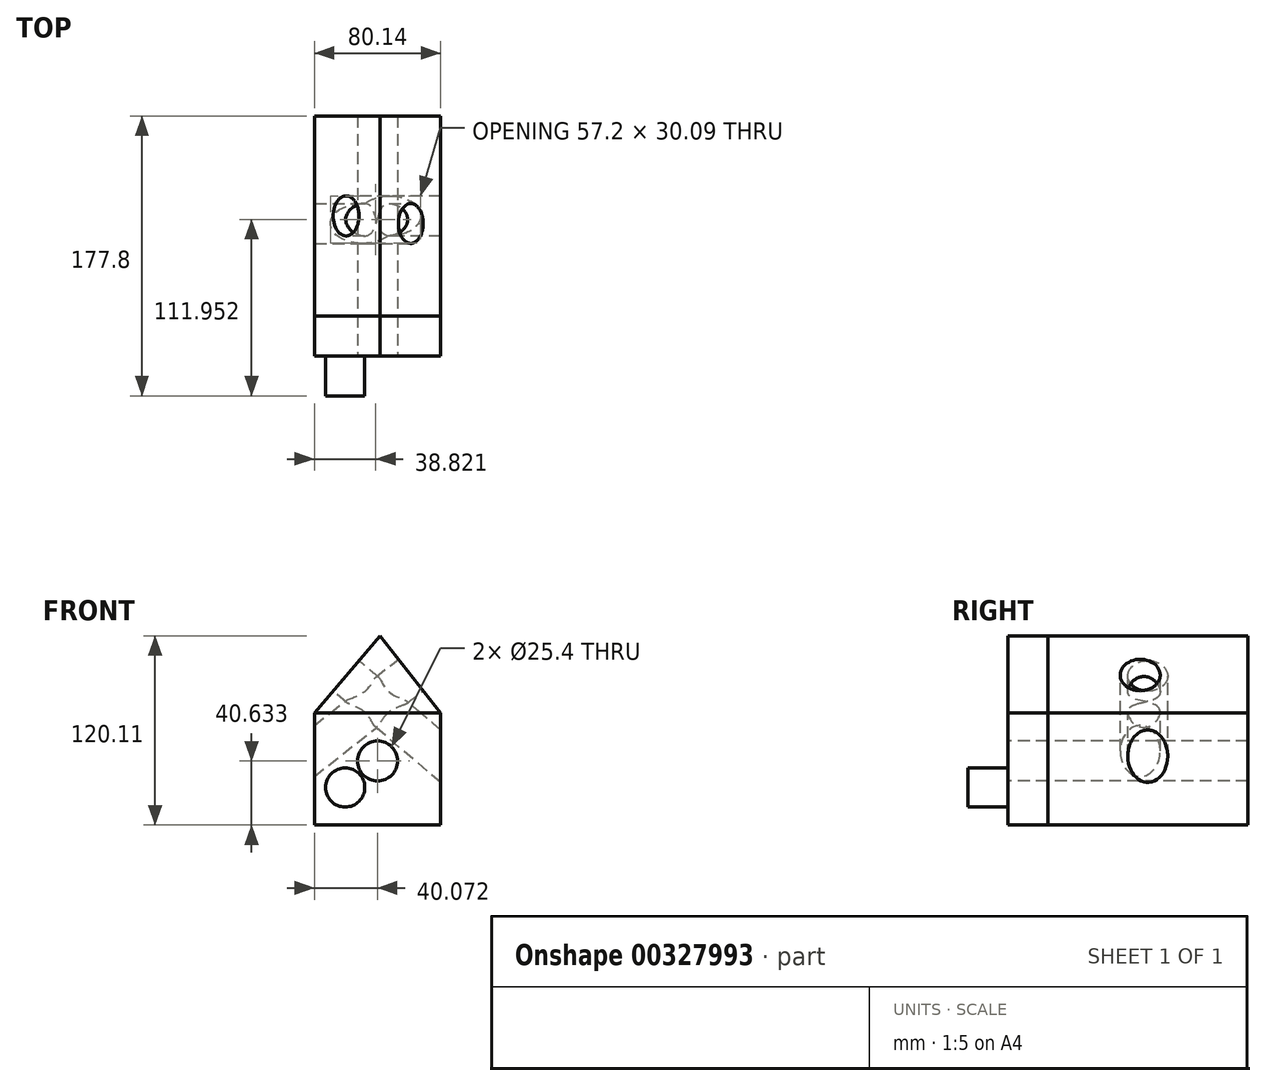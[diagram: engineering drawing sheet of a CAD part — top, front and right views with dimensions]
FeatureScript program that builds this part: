
annotation { "Feature Type Name" : "Feature", "Feature Type Description" : "" }
export const myFeature = defineFeature(function(context is Context, id is Id, definition is map)
    precondition{}
    {
        {
            var Q0;
            Q0=qCreatedBy(makeId("Front.planeOp"),FACE);
            var sketch = newSketch(context, id + "F0", { "sketchPlane" : qUnion([Q0])});
            skLineSegment(sketch, "E0.bottom", {"start": v(-274.23, -72.35) * mm, "end": v(-194.09, -72.35) * mm});
            skLineSegment(sketch, "E0.top", {"start": v(-274.23, -143.53) * mm, "end": v(-194.09, -143.53) * mm});
            skLineSegment(sketch, "E0.left", {"start": v(-274.23, -72.35) * mm, "end": v(-274.23, -143.53) * mm});
            skLineSegment(sketch, "E0.right", {"start": v(-194.09, -72.35) * mm, "end": v(-194.09, -143.53) * mm});
            skSolve(sketch);
        }
        {
            var Q0;
            Q0=makeQuery(id+"F0.imprint","IMPRINT",FACE,{"disambiguationData":[TD([[makeQuery(id+"F0.imprint","IMPRINT",EDGE,{"derivedFrom":sQuery(id+"F0.wireOp",EDGE,"E0.bottom")}),-1.0]])]});
            extrude(context, id + "F1", {"entities" : qUnion([Q0]), "depth" : 127 * mm});
        }
        {
            var Q0;
            Q0=makeQuery(id+"F1.opExtrude","CAP_FACE",FACE,{"disambiguationData":[OSD([sQuery(id+"F0.wireOp",EDGE,"E0.bottom"),sQuery(id+"F0.wireOp",EDGE,"E0.top"),sQuery(id+"F0.wireOp",EDGE,"E0.left"),sQuery(id+"F0.wireOp",EDGE,"E0.right")])],"isStart":false});
            var sketch = newSketch(context, id + "F2", { "sketchPlane" : qUnion([Q0])});
            skLineSegment(sketch, "E1", {"start": v(-274.23, -72.35) * mm, "end": v(-232.7, -23.42) * mm});
            skLineSegment(sketch, "E2", {"start": v(-232.7, -23.42) * mm, "end": v(-194.09, -72.35) * mm});
            skLineSegment(sketch, "E3", {"start": v(-194.09, -72.35) * mm, "end": v(-274.23, -72.35) * mm});
            skSolve(sketch);
        }
        {
            var Q0;
            Q0=makeQuery(id+"F2.imprint","IMPRINT",FACE,{"disambiguationData":[TD([[makeQuery(id+"F2.imprint","IMPRINT",EDGE,{"derivedFrom":sQuery(id+"F2.wireOp",EDGE,"E1")}),-1.0]])]});
            extrude(context, id + "F3", {"entities" : qUnion([Q0]), "depth" : 25.4 * mm});
        }
        {
            var Q0;
            Q0=makeQuery(id+"F3.opExtrude","CAP_FACE",FACE,{"disambiguationData":[OSD([sQuery(id+"F2.wireOp",EDGE,"E1"),sQuery(id+"F2.wireOp",EDGE,"E2"),sQuery(id+"F2.wireOp",EDGE,"E3")])],"isStart":true});
            extrude(context, id + "F4", {"entities" : qUnion([Q0]), "depth" : 127 * mm});
        }
        {
            var Q0;
            Q0=makeQuery(id+"F1.opExtrude","CAP_FACE",FACE,{"disambiguationData":[OSD([sQuery(id+"F0.wireOp",EDGE,"E0.bottom"),sQuery(id+"F0.wireOp",EDGE,"E0.top"),sQuery(id+"F0.wireOp",EDGE,"E0.left"),sQuery(id+"F0.wireOp",EDGE,"E0.right")])],"isStart":false});
            extrude(context, id + "F5", {"entities" : qUnion([Q0]), "depth" : 25.4 * mm});
        }
        {
            var Q0;
            Q0=makeQuery(id+"F3.opExtrude","CAP_FACE",FACE,{"disambiguationData":[OSD([sQuery(id+"F2.wireOp",EDGE,"E1"),sQuery(id+"F2.wireOp",EDGE,"E2"),sQuery(id+"F2.wireOp",EDGE,"E3")])],"isStart":false});
            var sketch = newSketch(context, id + "F6", { "sketchPlane" : qUnion([Q0])});
            skCircle(sketch, "E4", {"center": v(-254.74, -119.68) * mm, "radius": 12.45 * mm});
            skSolve(sketch);
        }
        {
            var Q0;
            Q0=makeQuery(id+"F6.imprint","IMPRINT",FACE,{"disambiguationData":[TD([[makeQuery(id+"F6.imprint","IMPRINT",EDGE,{"derivedFrom":sQuery(id+"F6.wireOp",EDGE,"E4")}),1.0]])]});
            extrude(context, id + "F7", {"entities" : qUnion([Q0]), "operationType" : NewBodyOperationType.ADD, "depth" : 25.4 * mm});
        }
        {
            var Q0;
            Q0=makeQuery(id+"F5.opExtrude","CAP_FACE",FACE,{"disambiguationData":[OSD([sQuery(id+"F0.wireOp",EDGE,"E0.bottom"),sQuery(id+"F0.wireOp",EDGE,"E0.top"),sQuery(id+"F0.wireOp",EDGE,"E0.left"),sQuery(id+"F0.wireOp",EDGE,"E0.right")])],"isStart":false});
            var sketch = newSketch(context, id + "F8", { "sketchPlane" : qUnion([Q0])});
            skCircle(sketch, "E5", {"center": v(-234.16, -102.9) * mm, "radius": 12.7 * mm});
            skSolve(sketch);
        }
        {
            var Q0;
            Q0=sQuery(id+"F8.wireOp",VERTEX,"E5.center");
            var Q1;
            Q1=makeQuery(id+"F5.opExtrude","SWEPT_BODY",BODY,{"disambiguationData":[OSD([sQuery(id+"F0.wireOp",EDGE,"E0.bottom"),sQuery(id+"F0.wireOp",EDGE,"E0.top"),sQuery(id+"F0.wireOp",EDGE,"E0.left"),sQuery(id+"F0.wireOp",EDGE,"E0.right")])]});
            var Q2;
            Q2=makeQuery(id+"F1.opExtrude","SWEPT_BODY",BODY,{"disambiguationData":[OSD([sQuery(id+"F0.wireOp",EDGE,"E0.bottom"),sQuery(id+"F0.wireOp",EDGE,"E0.top"),sQuery(id+"F0.wireOp",EDGE,"E0.left"),sQuery(id+"F0.wireOp",EDGE,"E0.right")])]});
            hole(context, id + "F9", {"style" : HoleStyle.SIMPLE, "endStyle" : HoleEndStyle.BLIND, "holeDiameter" : 25.4 * mm, "holeDepth" : 254 * mm, "tappedDepth" : 12.7 * mm, "tapClearance" : 3, "startFromSketch" : true, "locations" : qUnion([Q0]), "scope" : qUnion([Q1, Q2])});
        }
        {
            var Q0;
            Q0=makeQuery(id+"F4.opExtrude","SWEPT_FACE",FACE,{"disambiguationData":[OSD([sQuery(id+"F2.wireOp",EDGE,"E2")])]});
            var sketch = newSketch(context, id + "F10", { "sketchPlane" : qUnion([Q0])});
            skCircle(sketch, "E6", {"center": v(-68.3, 94.12) * mm, "radius": 19.23 * mm});
            skSolve(sketch);
        }
        {
            var Q0;
            Q0=sQuery(id+"F10.wireOp",VERTEX,"E6.center");
            var Q1;
            Q1=makeQuery(id+"F1.opExtrude","SWEPT_BODY",BODY,{"disambiguationData":[OSD([sQuery(id+"F0.wireOp",EDGE,"E0.bottom"),sQuery(id+"F0.wireOp",EDGE,"E0.top"),sQuery(id+"F0.wireOp",EDGE,"E0.left"),sQuery(id+"F0.wireOp",EDGE,"E0.right")])]});
            var Q2;
            Q2=makeQuery(id+"F4.opExtrude","SWEPT_BODY",BODY,{"disambiguationData":[OSD([sQuery(id+"F2.wireOp",EDGE,"E1"),sQuery(id+"F2.wireOp",EDGE,"E2"),sQuery(id+"F2.wireOp",EDGE,"E3")])]});
            hole(context, id + "F11", {"style" : HoleStyle.SIMPLE, "endStyle" : HoleEndStyle.BLIND, "holeDiameter" : 25.4 * mm, "holeDepth" : 254 * mm, "tappedDepth" : 12.7 * mm, "tapClearance" : 3, "startFromSketch" : true, "locations" : qUnion([Q0]), "scope" : qUnion([Q1, Q2])});
        }
        {
            var Q0;
            Q0=makeQuery(id+"F4.opExtrude","SWEPT_FACE",FACE,{"disambiguationData":[OSD([sQuery(id+"F2.wireOp",EDGE,"E1")])]});
            var sketch = newSketch(context, id + "F12", { "sketchPlane" : qUnion([Q0])});
            skCircle(sketch, "E7", {"center": v(63.5, -201.7) * mm, "radius": 12.7 * mm});
            skPoint(sketch, "E7.centerSnap0", {"position": v(63.5, -168.44) * mm});
            skSolve(sketch);
        }
        {
            var Q0;
            Q0=sQuery(id+"F12.wireOp",VERTEX,"E7.center");
            var Q1;
            Q1=makeQuery(id+"F1.opExtrude","SWEPT_BODY",BODY,{"disambiguationData":[OSD([sQuery(id+"F0.wireOp",EDGE,"E0.bottom"),sQuery(id+"F0.wireOp",EDGE,"E0.top"),sQuery(id+"F0.wireOp",EDGE,"E0.left"),sQuery(id+"F0.wireOp",EDGE,"E0.right")])]});
            var Q2;
            Q2=makeQuery(id+"F4.opExtrude","SWEPT_BODY",BODY,{"disambiguationData":[OSD([sQuery(id+"F2.wireOp",EDGE,"E1"),sQuery(id+"F2.wireOp",EDGE,"E2"),sQuery(id+"F2.wireOp",EDGE,"E3")])]});
            hole(context, id + "F13", {"style" : HoleStyle.SIMPLE, "endStyle" : HoleEndStyle.BLIND, "holeDiameter" : 25.4 * mm, "holeDepth" : 254 * mm, "tappedDepth" : 12.7 * mm, "tapClearance" : 3, "startFromSketch" : true, "locations" : qUnion([Q0]), "scope" : qUnion([Q1, Q2])});
        }
    });
